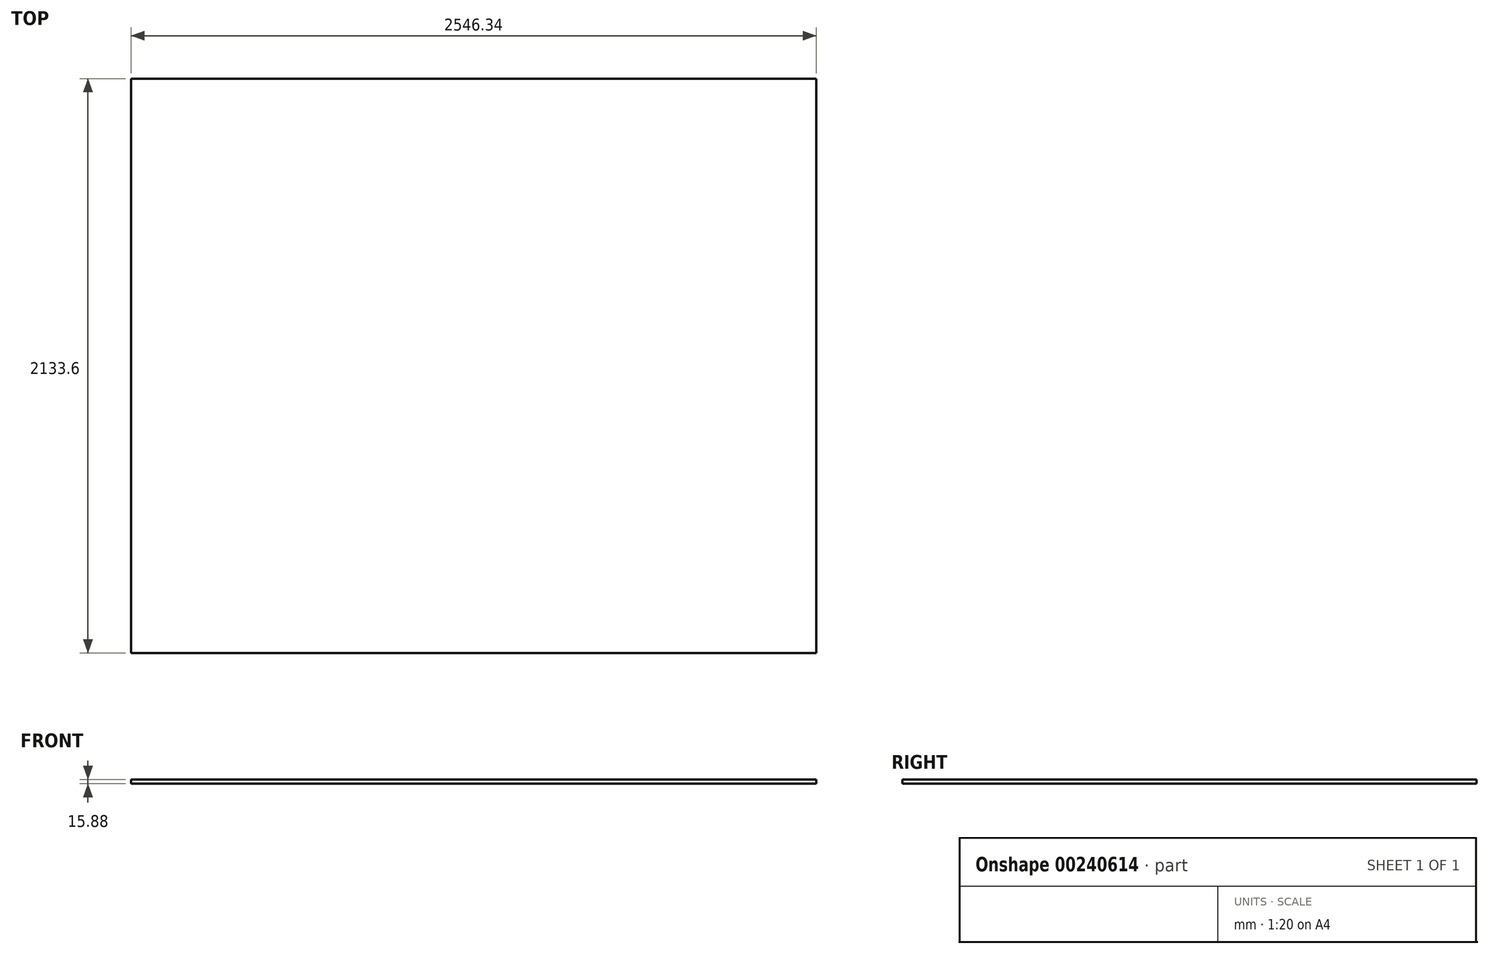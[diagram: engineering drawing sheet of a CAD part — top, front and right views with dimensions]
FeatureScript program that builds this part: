
annotation { "Feature Type Name" : "Feature", "Feature Type Description" : "" }
export const myFeature = defineFeature(function(context is Context, id is Id, definition is map)
    precondition{}
    {
        {
            var Q0;
            Q0=qCreatedBy(makeId("Top.planeOp"),FACE);
            var sketch = newSketch(context, id + "F0", { "sketchPlane" : qUnion([Q0])});
            skLineSegment(sketch, "E0.bottom", {"start": v(-1273.18, 1066.8) * mm, "end": v(1273.18, 1066.8) * mm});
            skLineSegment(sketch, "E0.top", {"start": v(-1273.18, -1066.8) * mm, "end": v(1273.18, -1066.8) * mm});
            skLineSegment(sketch, "E0.left", {"start": v(-1273.18, 1066.8) * mm, "end": v(-1273.18, -1066.8) * mm});
            skLineSegment(sketch, "E0.right", {"start": v(1273.18, 1066.8) * mm, "end": v(1273.18, -1066.8) * mm});
            skSolve(sketch);
        }
        {
            var Q0;
            Q0=makeQuery(id+"F0.imprint","IMPRINT",FACE,{"disambiguationData":[TD([[makeQuery(id+"F0.imprint","IMPRINT",EDGE,{"derivedFrom":sQuery(id+"F0.wireOp",EDGE,"E0.bottom")}),-1.0]])]});
            extrude(context, id + "F1", {"entities" : qUnion([Q0]), "depth" : 15.88 * mm, "offsetDistance" : 25.4 * mm});
        }
    });
